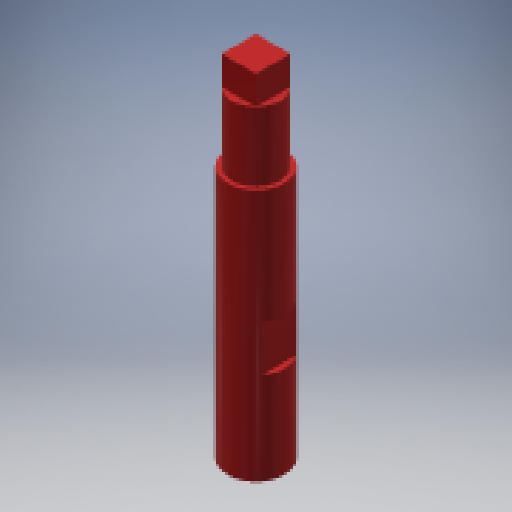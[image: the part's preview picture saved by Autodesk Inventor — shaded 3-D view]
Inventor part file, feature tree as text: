
AUTODESK INVENTOR PART (.ipt)
format: ipt  version: 2024.3 (Build 283343000, 343)  size: 296,960 bytes
history: native  units: mm
features: extrude x4, sketch x4, hole x1, projected_geometry x1
ambient origin geometry x8: Origin, YZ Plane, XZ Plane, XY Plane, X Axis, Y Axis, Z Axis, Center Point
bodies: Volumenkörper1 (feature_tree)
feature tree (10):
  extrude  "Extrusion1"  Depth=44.0mm TaperAngle=0.0deg
  extrude  "Extrusion2"  Depth=11.0mm TaperAngle=0.0deg
  hole  "Bohrung1"  [1 undecoded]
  extrude  "Extrusion3"  Depth=5.0mm TaperAngle=0.0deg
  extrude  "Extrusion4"  Depth=8.0mm
  sketch  "Skizze2"  dims[d0=10.0mm d1=44.0mm d2=0.0mm]
  sketch  "Skizze3"  dims[d3=8.5mm d4=11.0mm d5=0.0mm]
  sketch  "Skizze4"  dims[d6=4.134mm d7=10.0mm d8=4.0mm d9=2.0mm d10=90.0deg d11=14.2mm d12=20.594885mm d13=6.0mm]
  sketch  "Skizze5"  dims[d14=6.0mm d15=5.0mm d16=0.0mm d17=8.0mm d18=8.0mm d19=20.0mm d20=44.0mm d21=0.0mm]
  projected_geometry  "Projizierte Kontur1"
note: 1 required parameter value undecoded (feature->parameter linkage not recoverable at this tier; creation-order binding heuristic only, values carry confidence <= 0.55)
